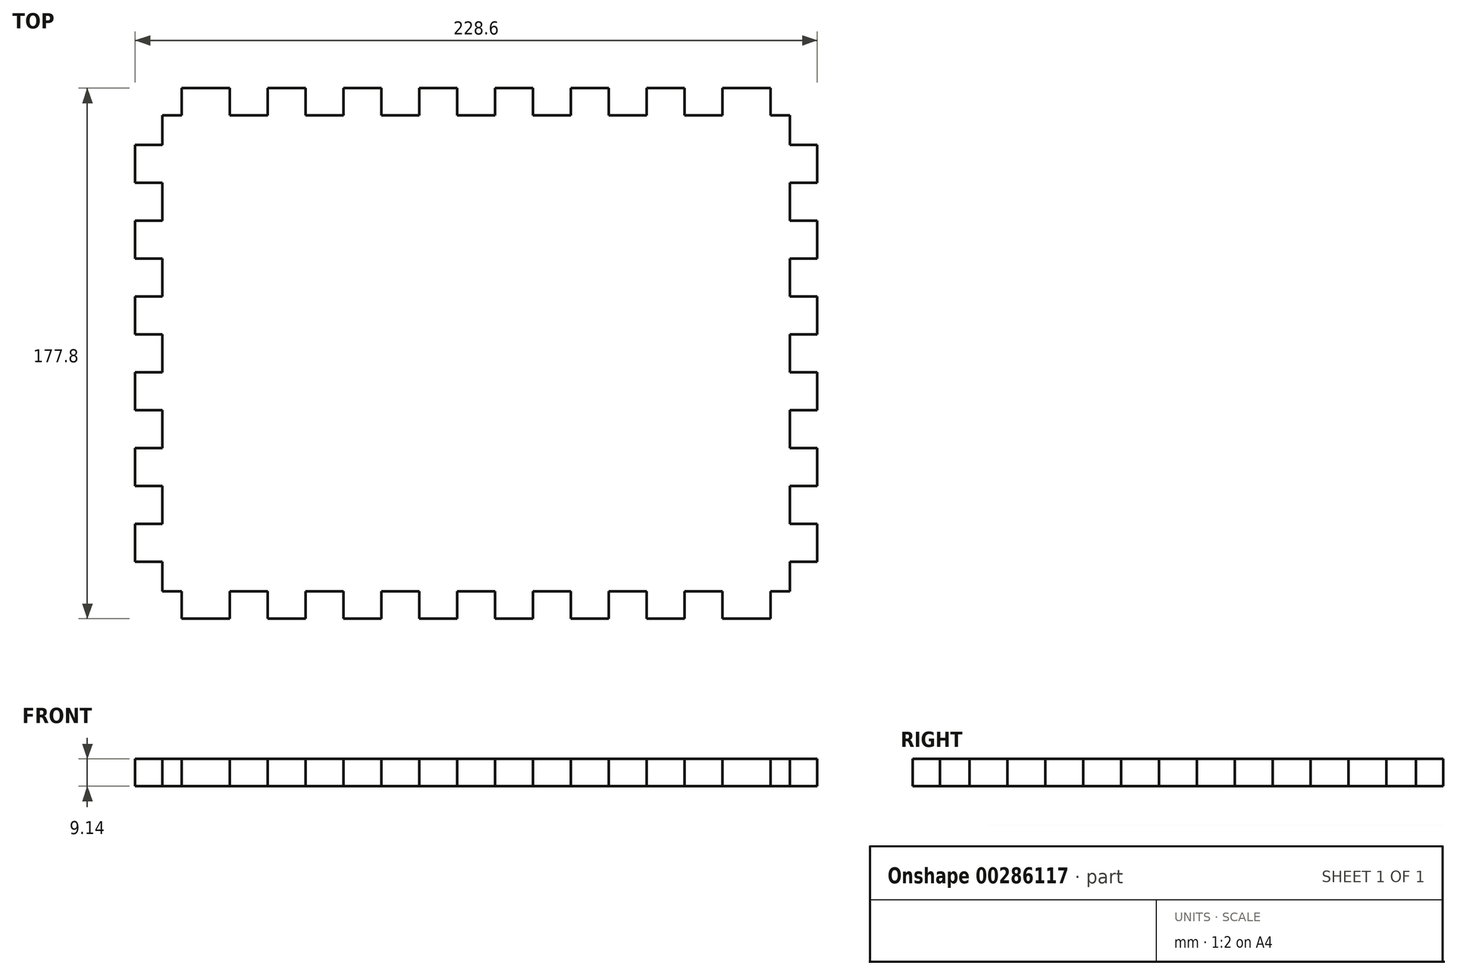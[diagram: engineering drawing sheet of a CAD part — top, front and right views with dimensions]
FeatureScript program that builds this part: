
annotation { "Feature Type Name" : "Feature", "Feature Type Description" : "" }
export const myFeature = defineFeature(function(context is Context, id is Id, definition is map)
    precondition{}
    {
        {
            var Q0;
            Q0=qCreatedBy(makeId("Top.planeOp"),FACE);
            var sketch = newSketch(context, id + "F0", { "sketchPlane" : qUnion([Q0])});
            skLineSegment(sketch, "E0", {"start": v(15.6, 0) * mm, "end": v(15.6, -9.14) * mm});
            skLineSegment(sketch, "E1", {"start": v(15.6, -9.14) * mm, "end": v(9.14, -9.14) * mm});
            skLineSegment(sketch, "E2", {"start": v(9.14, -9.14) * mm, "end": v(9.14, -19.05) * mm});
            skLineSegment(sketch, "E3", {"start": v(9.14, -19.05) * mm, "end": v(0, -19.05) * mm});
            skLineSegment(sketch, "E4", {"start": v(15.6, 0) * mm, "end": v(0, 0) * mm, "construction": true});
            skLineSegment(sketch, "E5", {"start": v(15.6, 0) * mm, "end": v(31.75, 0) * mm});
            skLineSegment(sketch, "E6", {"start": v(31.75, 0) * mm, "end": v(31.75, -9.14) * mm});
            skLineSegment(sketch, "E7", {"start": v(31.75, -9.14) * mm, "end": v(44.45, -9.14) * mm});
            skLineSegment(sketch, "E8", {"start": v(44.45, -9.14) * mm, "end": v(44.45, 0) * mm});
            skLineSegment(sketch, "E9", {"start": v(44.45, 0) * mm, "end": v(57.15, 0) * mm});
            skLineSegment(sketch, "E10", {"start": v(114.3, -88.9) * mm, "end": v(114.3, 0) * mm, "construction": true});
            skLineSegment(sketch, "E11", {"start": v(57.15, 0) * mm, "end": v(57.15, -9.14) * mm});
            skLineSegment(sketch, "E12", {"start": v(57.15, -9.14) * mm, "end": v(69.85, -9.14) * mm});
            skLineSegment(sketch, "E13", {"start": v(69.85, 0) * mm, "end": v(69.85, -9.14) * mm});
            skLineSegment(sketch, "E14", {"start": v(69.85, 0) * mm, "end": v(82.55, 0) * mm});
            skLineSegment(sketch, "E15", {"start": v(82.55, -9.14) * mm, "end": v(82.55, 0) * mm});
            skLineSegment(sketch, "E16", {"start": v(82.55, -9.14) * mm, "end": v(95.25, -9.14) * mm});
            skLineSegment(sketch, "E17", {"start": v(95.25, 0) * mm, "end": v(95.25, -9.14) * mm});
            skLineSegment(sketch, "E18", {"start": v(95.25, 0) * mm, "end": v(107.95, 0) * mm});
            skLineSegment(sketch, "E19", {"start": v(107.95, -9.14) * mm, "end": v(107.95, 0) * mm});
            skLineSegment(sketch, "E20", {"start": v(107.95, -9.14) * mm, "end": v(114.3, -9.14) * mm});
            skLineSegment(sketch, "E21", {"start": v(0, -88.9) * mm, "end": v(114.3, -88.9) * mm, "construction": true});
            skLineSegment(sketch, "E22", {"start": v(0, 0) * mm, "end": v(0, -19.05) * mm, "construction": true});
            skLineSegment(sketch, "E23", {"start": v(0, -19.05) * mm, "end": v(0, -31.75) * mm});
            skLineSegment(sketch, "E24", {"start": v(0, -31.75) * mm, "end": v(9.14, -31.75) * mm});
            skLineSegment(sketch, "E25", {"start": v(9.14, -44.45) * mm, "end": v(9.14, -31.75) * mm});
            skLineSegment(sketch, "E26", {"start": v(9.14, -44.45) * mm, "end": v(0, -44.45) * mm});
            skLineSegment(sketch, "E27", {"start": v(0, -44.45) * mm, "end": v(0, -57.15) * mm});
            skLineSegment(sketch, "E28", {"start": v(0, -57.15) * mm, "end": v(9.14, -57.15) * mm});
            skLineSegment(sketch, "E29", {"start": v(9.14, -69.85) * mm, "end": v(9.14, -57.15) * mm});
            skLineSegment(sketch, "E30", {"start": v(9.14, -69.85) * mm, "end": v(0, -69.85) * mm});
            skLineSegment(sketch, "E31", {"start": v(0, -82.55) * mm, "end": v(0, -69.85) * mm});
            skLineSegment(sketch, "E32", {"start": v(0, -82.55) * mm, "end": v(9.14, -82.55) * mm});
            skLineSegment(sketch, "E33", {"start": v(9.14, -82.55) * mm, "end": v(9.14, -88.9) * mm});
            skLineSegment(sketch, "E34.MirrorCS", {"start": v(107.95, -168.66) * mm, "end": v(107.95, -177.8) * mm});
            skLineSegment(sketch, "E35.MirrorCS", {"start": v(82.55, -168.66) * mm, "end": v(82.55, -177.8) * mm});
            skLineSegment(sketch, "E36.MirrorCS", {"start": v(15.6, -177.8) * mm, "end": v(15.6, -168.66) * mm});
            skLineSegment(sketch, "E37.MirrorCS", {"start": v(69.85, -177.8) * mm, "end": v(69.85, -168.66) * mm});
            skLineSegment(sketch, "E38.MirrorCS", {"start": v(31.75, -177.8) * mm, "end": v(31.75, -168.66) * mm});
            skLineSegment(sketch, "E39.MirrorCS", {"start": v(15.6, -168.66) * mm, "end": v(9.14, -168.66) * mm});
            skLineSegment(sketch, "E40.MirrorCS", {"start": v(95.25, -177.8) * mm, "end": v(95.25, -168.66) * mm});
            skLineSegment(sketch, "E41.MirrorCS", {"start": v(57.15, -177.8) * mm, "end": v(57.15, -168.66) * mm});
            skLineSegment(sketch, "E42.MirrorCS", {"start": v(44.45, -168.66) * mm, "end": v(44.45, -177.8) * mm});
            skLineSegment(sketch, "E43.MirrorCS", {"start": v(107.95, -168.66) * mm, "end": v(114.3, -168.66) * mm});
            skLineSegment(sketch, "E44.MirrorCS", {"start": v(44.45, -177.8) * mm, "end": v(57.15, -177.8) * mm});
            skLineSegment(sketch, "E45.MirrorCS", {"start": v(15.6, -177.8) * mm, "end": v(31.75, -177.8) * mm});
            skLineSegment(sketch, "E46.MirrorCS", {"start": v(9.14, -107.95) * mm, "end": v(9.14, -120.65) * mm});
            skLineSegment(sketch, "E47.MirrorCS", {"start": v(0, -177.8) * mm, "end": v(0, -158.75) * mm, "construction": true});
            skLineSegment(sketch, "E48.MirrorCS", {"start": v(9.14, -158.75) * mm, "end": v(0, -158.75) * mm});
            skLineSegment(sketch, "E49.MirrorCS", {"start": v(0, -95.25) * mm, "end": v(0, -107.95) * mm});
            skLineSegment(sketch, "E50.MirrorCS", {"start": v(9.14, -133.35) * mm, "end": v(9.14, -146.05) * mm});
            skLineSegment(sketch, "E51.MirrorCS", {"start": v(9.14, -133.35) * mm, "end": v(0, -133.35) * mm});
            skLineSegment(sketch, "E52.MirrorCS", {"start": v(0, -95.25) * mm, "end": v(9.14, -95.25) * mm});
            skLineSegment(sketch, "E53.MirrorCS", {"start": v(15.6, -177.8) * mm, "end": v(0, -177.8) * mm, "construction": true});
            skLineSegment(sketch, "E54.MirrorCS", {"start": v(0, -146.05) * mm, "end": v(9.14, -146.05) * mm});
            skLineSegment(sketch, "E55.MirrorCS", {"start": v(9.14, -107.95) * mm, "end": v(0, -107.95) * mm});
            skLineSegment(sketch, "E56.MirrorCS", {"start": v(57.15, -168.66) * mm, "end": v(69.85, -168.66) * mm});
            skLineSegment(sketch, "E57.MirrorCS", {"start": v(9.14, -168.66) * mm, "end": v(9.14, -158.75) * mm});
            skLineSegment(sketch, "E58.MirrorCS", {"start": v(0, -158.75) * mm, "end": v(0, -146.05) * mm});
            skLineSegment(sketch, "E59.MirrorCS", {"start": v(95.25, -177.8) * mm, "end": v(107.95, -177.8) * mm});
            skLineSegment(sketch, "E60.MirrorCS", {"start": v(69.85, -177.8) * mm, "end": v(82.55, -177.8) * mm});
            skLineSegment(sketch, "E61.MirrorCS", {"start": v(0, -120.65) * mm, "end": v(9.14, -120.65) * mm});
            skLineSegment(sketch, "E62.MirrorCS", {"start": v(31.75, -168.66) * mm, "end": v(44.45, -168.66) * mm});
            skLineSegment(sketch, "E63.MirrorCS", {"start": v(0, -133.35) * mm, "end": v(0, -120.65) * mm});
            skLineSegment(sketch, "E64.MirrorCS", {"start": v(82.55, -168.66) * mm, "end": v(95.25, -168.66) * mm});
            skLineSegment(sketch, "E65.MirrorCS", {"start": v(9.14, -95.25) * mm, "end": v(9.14, -88.9) * mm});
            skLineSegment(sketch, "E66.MirrorCS", {"start": v(219.46, -82.55) * mm, "end": v(219.46, -88.9) * mm});
            skLineSegment(sketch, "E67.MirrorCS", {"start": v(213, -9.14) * mm, "end": v(219.46, -9.14) * mm});
            skLineSegment(sketch, "E68.MirrorCS", {"start": v(219.46, -95.25) * mm, "end": v(219.46, -88.9) * mm});
            skLineSegment(sketch, "E69.MirrorCS", {"start": v(228.6, -95.25) * mm, "end": v(219.46, -95.25) * mm});
            skLineSegment(sketch, "E70.MirrorCS", {"start": v(219.46, -158.75) * mm, "end": v(228.6, -158.75) * mm});
            skLineSegment(sketch, "E71.MirrorCS", {"start": v(219.46, -9.14) * mm, "end": v(219.46, -19.05) * mm});
            skLineSegment(sketch, "E72.MirrorCS", {"start": v(228.6, -82.55) * mm, "end": v(219.46, -82.55) * mm});
            skLineSegment(sketch, "E73.MirrorCS", {"start": v(213, 0) * mm, "end": v(213, -9.14) * mm});
            skLineSegment(sketch, "E74.MirrorCS", {"start": v(120.65, -9.14) * mm, "end": v(114.3, -9.14) * mm});
            skLineSegment(sketch, "E75.MirrorCS", {"start": v(228.6, -133.35) * mm, "end": v(228.6, -120.65) * mm});
            skLineSegment(sketch, "E76.MirrorCS", {"start": v(219.46, -69.85) * mm, "end": v(219.46, -57.15) * mm});
            skLineSegment(sketch, "E77.MirrorCS", {"start": v(133.35, 0) * mm, "end": v(120.65, 0) * mm});
            skLineSegment(sketch, "E78.MirrorCS", {"start": v(146.05, -168.66) * mm, "end": v(146.05, -177.8) * mm});
            skLineSegment(sketch, "E79.MirrorCS", {"start": v(184.15, -177.8) * mm, "end": v(171.45, -177.8) * mm});
            skLineSegment(sketch, "E80.MirrorCS", {"start": v(184.15, -9.14) * mm, "end": v(184.15, 0) * mm});
            skLineSegment(sketch, "E81.MirrorCS", {"start": v(196.85, -9.14) * mm, "end": v(184.15, -9.14) * mm});
            skLineSegment(sketch, "E82.MirrorCS", {"start": v(158.75, 0) * mm, "end": v(146.05, 0) * mm});
            skLineSegment(sketch, "E83.MirrorCS", {"start": v(196.85, 0) * mm, "end": v(196.85, -9.14) * mm});
            skLineSegment(sketch, "E84.MirrorCS", {"start": v(219.46, -19.05) * mm, "end": v(228.6, -19.05) * mm});
            skLineSegment(sketch, "E85.MirrorCS", {"start": v(133.35, 0) * mm, "end": v(133.35, -9.14) * mm});
            skLineSegment(sketch, "E86.MirrorCS", {"start": v(219.46, -107.95) * mm, "end": v(219.46, -120.65) * mm});
            skLineSegment(sketch, "E87.MirrorCS", {"start": v(158.75, -177.8) * mm, "end": v(146.05, -177.8) * mm});
            skLineSegment(sketch, "E88.MirrorCS", {"start": v(213, -177.8) * mm, "end": v(213, -168.66) * mm});
            skLineSegment(sketch, "E89.MirrorCS", {"start": v(196.85, -177.8) * mm, "end": v(196.85, -168.66) * mm});
            skLineSegment(sketch, "E90.MirrorCS", {"start": v(228.6, -57.15) * mm, "end": v(219.46, -57.15) * mm});
            skLineSegment(sketch, "E91.MirrorCS", {"start": v(213, 0) * mm, "end": v(196.85, 0) * mm});
            skLineSegment(sketch, "E92.MirrorCS", {"start": v(146.05, -168.66) * mm, "end": v(133.35, -168.66) * mm});
            skLineSegment(sketch, "E93.MirrorCS", {"start": v(213, 0) * mm, "end": v(228.6, 0) * mm, "construction": true});
            skLineSegment(sketch, "E94.MirrorCS", {"start": v(228.6, -158.75) * mm, "end": v(228.6, -146.05) * mm});
            skLineSegment(sketch, "E95.MirrorCS", {"start": v(219.46, -44.45) * mm, "end": v(228.6, -44.45) * mm});
            skLineSegment(sketch, "E96.MirrorCS", {"start": v(184.15, -168.66) * mm, "end": v(184.15, -177.8) * mm});
            skLineSegment(sketch, "E97.MirrorCS", {"start": v(120.65, -9.14) * mm, "end": v(120.65, 0) * mm});
            skLineSegment(sketch, "E98.MirrorCS", {"start": v(219.46, -133.35) * mm, "end": v(228.6, -133.35) * mm});
            skLineSegment(sketch, "E99.MirrorCS", {"start": v(228.6, -120.65) * mm, "end": v(219.46, -120.65) * mm});
            skLineSegment(sketch, "E100.MirrorCS", {"start": v(158.75, -177.8) * mm, "end": v(158.75, -168.66) * mm});
            skLineSegment(sketch, "E101.MirrorCS", {"start": v(228.6, -146.05) * mm, "end": v(219.46, -146.05) * mm});
            skLineSegment(sketch, "E102.MirrorCS", {"start": v(228.6, -19.05) * mm, "end": v(228.6, -31.75) * mm});
            skLineSegment(sketch, "E103.MirrorCS", {"start": v(213, -168.66) * mm, "end": v(219.46, -168.66) * mm});
            skLineSegment(sketch, "E104.MirrorCS", {"start": v(219.46, -107.95) * mm, "end": v(228.6, -107.95) * mm});
            skLineSegment(sketch, "E105.MirrorCS", {"start": v(120.65, -168.66) * mm, "end": v(114.3, -168.66) * mm});
            skLineSegment(sketch, "E106.MirrorCS", {"start": v(228.6, -44.45) * mm, "end": v(228.6, -57.15) * mm});
            skLineSegment(sketch, "E107.MirrorCS", {"start": v(133.35, -177.8) * mm, "end": v(120.65, -177.8) * mm});
            skLineSegment(sketch, "E108.MirrorCS", {"start": v(171.45, -9.14) * mm, "end": v(158.75, -9.14) * mm});
            skLineSegment(sketch, "E109.MirrorCS", {"start": v(158.75, 0) * mm, "end": v(158.75, -9.14) * mm});
            skLineSegment(sketch, "E110.MirrorCS", {"start": v(171.45, 0) * mm, "end": v(171.45, -9.14) * mm});
            skLineSegment(sketch, "E111.MirrorCS", {"start": v(184.15, 0) * mm, "end": v(171.45, 0) * mm});
            skLineSegment(sketch, "E112.MirrorCS", {"start": v(171.45, -177.8) * mm, "end": v(171.45, -168.66) * mm});
            skLineSegment(sketch, "E113.MirrorCS", {"start": v(228.6, 0) * mm, "end": v(228.6, -19.05) * mm, "construction": true});
            skLineSegment(sketch, "E114.MirrorCS", {"start": v(213, -177.8) * mm, "end": v(228.6, -177.8) * mm, "construction": true});
            skLineSegment(sketch, "E115.MirrorCS", {"start": v(228.6, -82.55) * mm, "end": v(228.6, -69.85) * mm});
            skLineSegment(sketch, "E116.MirrorCS", {"start": v(146.05, -9.14) * mm, "end": v(146.05, 0) * mm});
            skLineSegment(sketch, "E117.MirrorCS", {"start": v(228.6, -31.75) * mm, "end": v(219.46, -31.75) * mm});
            skLineSegment(sketch, "E118.MirrorCS", {"start": v(219.46, -44.45) * mm, "end": v(219.46, -31.75) * mm});
            skLineSegment(sketch, "E119.MirrorCS", {"start": v(219.46, -69.85) * mm, "end": v(228.6, -69.85) * mm});
            skLineSegment(sketch, "E120.MirrorCS", {"start": v(146.05, -9.14) * mm, "end": v(133.35, -9.14) * mm});
            skLineSegment(sketch, "E121.MirrorCS", {"start": v(133.35, -177.8) * mm, "end": v(133.35, -168.66) * mm});
            skLineSegment(sketch, "E122.MirrorCS", {"start": v(196.85, -168.66) * mm, "end": v(184.15, -168.66) * mm});
            skLineSegment(sketch, "E123.MirrorCS", {"start": v(219.46, -168.66) * mm, "end": v(219.46, -158.75) * mm});
            skLineSegment(sketch, "E124.MirrorCS", {"start": v(228.6, -95.25) * mm, "end": v(228.6, -107.95) * mm});
            skLineSegment(sketch, "E125.MirrorCS", {"start": v(213, -177.8) * mm, "end": v(196.85, -177.8) * mm});
            skLineSegment(sketch, "E126.MirrorCS", {"start": v(120.65, -168.66) * mm, "end": v(120.65, -177.8) * mm});
            skLineSegment(sketch, "E127.MirrorCS", {"start": v(219.46, -133.35) * mm, "end": v(219.46, -146.05) * mm});
            skLineSegment(sketch, "E128.MirrorCS", {"start": v(171.45, -168.66) * mm, "end": v(158.75, -168.66) * mm});
            skLineSegment(sketch, "E129.MirrorCS", {"start": v(228.6, -177.8) * mm, "end": v(228.6, -158.75) * mm, "construction": true});
            skLineSegment(sketch, "E130.MirrorCS", {"start": v(228.6, -88.9) * mm, "end": v(114.3, -88.9) * mm, "construction": true});
            skSolve(sketch);
        }
        {
            var Q0;
            Q0=makeQuery(id+"F0.imprint","IMPRINT",FACE,{"disambiguationData":[TD([[makeQuery(id+"F0.imprint","IMPRINT",EDGE,{"derivedFrom":sQuery(id+"F0.wireOp",EDGE,"E0")}),1.0]])]});
            extrude(context, id + "F1", {"entities" : qUnion([Q0]), "depth" : 9.14 * mm});
        }
    });
